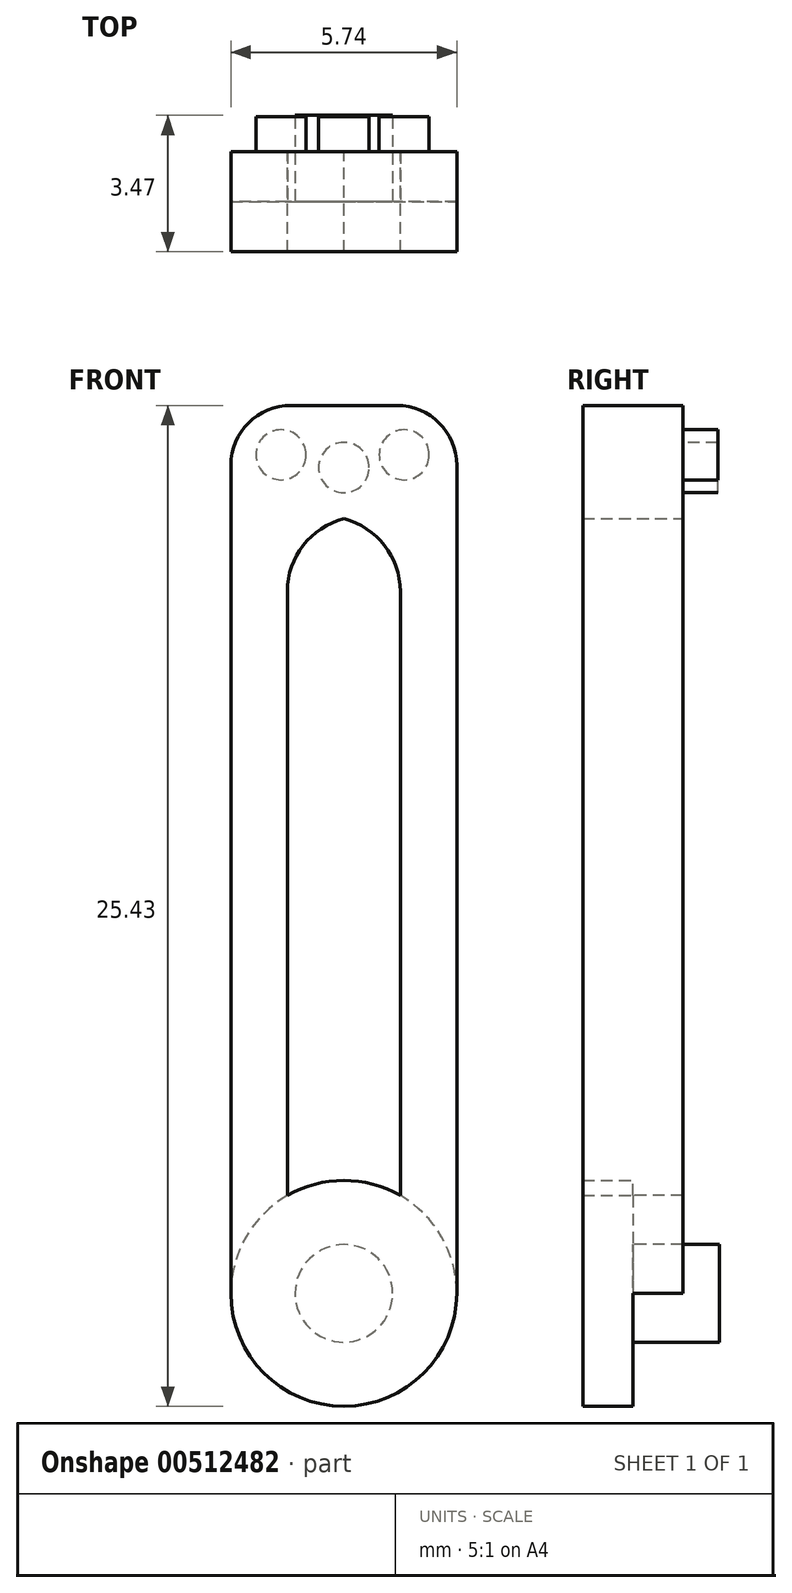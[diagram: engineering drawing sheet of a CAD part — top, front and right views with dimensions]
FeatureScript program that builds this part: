
annotation { "Feature Type Name" : "Feature", "Feature Type Description" : "" }
export const myFeature = defineFeature(function(context is Context, id is Id, definition is map)
    precondition{}
    {
        {
            var Q0;
            Q0=qCreatedBy(makeId("Front.planeOp"),FACE);
            var sketch = newSketch(context, id + "F0", { "sketchPlane" : qUnion([Q0])});
            skCircle(sketch, "E0", {"center": v(0, 2.87) * mm, "radius": 2.87 * mm});
            skLineSegment(sketch, "E1", {"start": v(0, 25.43) * mm, "end": v(2.87, 25.43) * mm});
            skLineSegment(sketch, "E2", {"start": v(2.87, 25.43) * mm, "end": v(2.87, 2.87) * mm});
            skLineSegment(sketch, "E3", {"start": v(-2.87, 2.87) * mm, "end": v(-2.87, 25.43) * mm});
            skLineSegment(sketch, "E4", {"start": v(-2.87, 25.43) * mm, "end": v(2.87, 25.43) * mm});
            skLineSegment(sketch, "E5", {"start": v(-2.87, 25.43) * mm, "end": v(0, 25.43) * mm});
            skLineSegment(sketch, "E6", {"start": v(-2.87, 25.43) * mm, "end": v(-1.43, 25.43) * mm});
            skLineSegment(sketch, "E7", {"start": v(1.43, 5.35) * mm, "end": v(1.43, 22.6) * mm});
            skLineSegment(sketch, "E8", {"start": v(-1.43, 5.35) * mm, "end": v(-1.43, 22.6) * mm});
            skLineSegment(sketch, "E9", {"start": v(-1.43, 22.6) * mm, "end": v(1.43, 22.6) * mm});
            skSolve(sketch);
        }
        {
            var Q0;
            {var subQ0=sQuery(id+"F0.wireOp",EDGE,"E2");Q0=makeQuery(id+"F0.imprint","IMPRINT",FACE,{"disambiguationData":[TD([[makeQuery(id+"F0.imprint","IMPRINT",EDGE,{"derivedFrom":subQ0}),-1.0]])]});}
            var Q1;
            {var subQ0=sQuery(id+"F0.wireOp",EDGE,"E0");var subQ1=makeQuery(id+"F0.imprint","INTERSECT",VERTEX,{"derivedFrom":[subQ0,sQuery(id+"F0.wireOp",EDGE,"E2")]});Q1=makeQuery(id+"F0.imprint","IMPRINT",FACE,{"disambiguationData":[TD([[makeQuery(id+"F0.imprint","IMPRINT",EDGE,{"disambiguationData":[TD([[subQ1,-1.0]])],"derivedFrom":subQ0}),1.0]])]});}
            extrude(context, id + "F1", {"entities" : qUnion([Q0, Q1]), "depth" : 1.27 * mm});
        }
        {
            var Q0;
            Q0=makeQuery(id+"F1.opExtrude","CAP_FACE",FACE,{"disambiguationData":[OSD([sQuery(id+"F0.wireOp",EDGE,"E0"),sQuery(id+"F0.wireOp",EDGE,"E2"),sQuery(id+"F0.wireOp",EDGE,"E3"),sQuery(id+"F0.wireOp",EDGE,"E4"),sQuery(id+"F0.wireOp",EDGE,"E5"),sQuery(id+"F0.wireOp",EDGE,"E6"),sQuery(id+"F0.wireOp",EDGE,"E7"),sQuery(id+"F0.wireOp",EDGE,"E8"),sQuery(id+"F0.wireOp",EDGE,"E9")])],"isStart":true});
            var sketch = newSketch(context, id + "F2", { "sketchPlane" : qUnion([Q0])});
            skCircle(sketch, "E10", {"center": v(0, 2.87) * mm, "radius": 1.24 * mm});
            skSolve(sketch);
        }
        {
            var Q0;
            Q0=makeQuery(id+"F1.opExtrude","SWEPT_EDGE",EDGE,{"disambiguationData":[OSD([sQuery(id+"F0.wireOp",EDGE,"E2"),sQuery(id+"F0.wireOp",EDGE,"E4")])]});
            var Q1;
            Q1=makeQuery(id+"F1.opExtrude","SWEPT_EDGE",EDGE,{"disambiguationData":[OSD([sQuery(id+"F0.wireOp",EDGE,"E3"),sQuery(id+"F0.wireOp",EDGE,"E6")])]});
            fillet(context, id + "F3", {"entities" : qUnion([Q0, Q1]), "radius" : 1.52 * mm, "tangentPropagation" : true, "allowEdgeOverflow" : false});
        }
        {
            var Q0;
            Q0=makeQuery(id+"F1.opExtrude","CAP_FACE",FACE,{"disambiguationData":[OSD([sQuery(id+"F0.wireOp",EDGE,"E0"),sQuery(id+"F0.wireOp",EDGE,"E2"),sQuery(id+"F0.wireOp",EDGE,"E3"),sQuery(id+"F0.wireOp",EDGE,"E4"),sQuery(id+"F0.wireOp",EDGE,"E5"),sQuery(id+"F0.wireOp",EDGE,"E6"),sQuery(id+"F0.wireOp",EDGE,"E7"),sQuery(id+"F0.wireOp",EDGE,"E8"),sQuery(id+"F0.wireOp",EDGE,"E9")])],"isStart":false});
            var sketch = newSketch(context, id + "F4", { "sketchPlane" : qUnion([Q0])});
            skPoint(sketch, "E11.startSnap0", {"position": v(-1.21, 23.8) * mm});
            skCircle(sketch, "E12", {"center": v(-1.6, 24.17) * mm, "radius": 0.64 * mm});
            skCircle(sketch, "E13", {"center": v(1.53, 24.17) * mm, "radius": 0.64 * mm});
            skCircle(sketch, "E14", {"center": v(0, 23.85) * mm, "radius": 0.64 * mm});
            skSolve(sketch);
        }
        {
            var Q0;
            Q0=makeQuery(id+"F1.opExtrude","SWEPT_EDGE",EDGE,{"disambiguationData":[OSD([sQuery(id+"F0.wireOp",EDGE,"E7"),sQuery(id+"F0.wireOp",EDGE,"E9")])]});
            var Q1;
            Q1=makeQuery(id+"F1.opExtrude","SWEPT_EDGE",EDGE,{"disambiguationData":[OSD([sQuery(id+"F0.wireOp",EDGE,"E8"),sQuery(id+"F0.wireOp",EDGE,"E9")])]});
            fillet(context, id + "F5", {"entities" : qUnion([Q0, Q1]), "radius" : 1.9 * mm, "tangentPropagation" : true, "allowEdgeOverflow" : false});
        }
        {
            var Q0;
            Q0 = qSketchRegion(id + "F2", true);
            extrude(context, id + "F6", {"entities" : qUnion([Q0]), "operationType" : NewBodyOperationType.ADD, "depth" : 2.2 * mm});
        }
        {
            var Q0;
            Q0 = qSketchRegion(id + "F4", true);
            extrude(context, id + "F7", {"entities" : qUnion([Q0]), "operationType" : NewBodyOperationType.ADD, "depth" : -3.43 * mm});
        }
        {
            var Q0;
            Q0=makeQuery(id+"F1.opExtrude","CAP_FACE",FACE,{"disambiguationData":[OSD([sQuery(id+"F0.wireOp",EDGE,"E0"),sQuery(id+"F0.wireOp",EDGE,"E2"),sQuery(id+"F0.wireOp",EDGE,"E3"),sQuery(id+"F0.wireOp",EDGE,"E4"),sQuery(id+"F0.wireOp",EDGE,"E5"),sQuery(id+"F0.wireOp",EDGE,"E6"),sQuery(id+"F0.wireOp",EDGE,"E7"),sQuery(id+"F0.wireOp",EDGE,"E8"),sQuery(id+"F0.wireOp",EDGE,"E9")])],"isStart":false});
            var sketch = newSketch(context, id + "F8", { "sketchPlane" : qUnion([Q0])});
            skCircle(sketch, "E15", {"center": v(0, 2.87) * mm, "radius": 2.87 * mm});
            skCircle(sketch, "E16", {"center": v(-1.34, 23.9) * mm, "radius": 1.52 * mm});
            skCircle(sketch, "E17", {"center": v(1.34, 23.9) * mm, "radius": 1.52 * mm});
            skLineSegment(sketch, "E18", {"start": v(-1.34, 25.43) * mm, "end": v(1.34, 25.43) * mm});
            skLineSegment(sketch, "E19", {"start": v(-2.87, 22.55) * mm, "end": v(-2.87, 2.87) * mm});
            skLineSegment(sketch, "E20", {"start": v(2.87, 2.87) * mm, "end": v(2.87, 23.9) * mm});
            skLineSegment(sketch, "E21", {"start": v(-1.43, 5.35) * mm, "end": v(-1.43, 20.7) * mm});
            skLineSegment(sketch, "E22", {"start": v(1.43, 5.35) * mm, "end": v(1.43, 20.7) * mm});
            skSolve(sketch);
        }
        {
            var Q0;
            {var subQ8=sQuery(id+"F8.wireOp",EDGE,"E19");Q0=makeQuery(id+"F8.imprint","IMPRINT",FACE,{"disambiguationData":[TD([[makeQuery(id+"F8.imprint","IMPRINT",EDGE,{"derivedFrom":subQ8}),-1.0]])]});}
            var Q1;
            {var subQ0=sQuery(id+"F8.wireOp",EDGE,"E16");var subQ1=makeQuery(id+"F8.imprint","INTERSECT",VERTEX,{"derivedFrom":[subQ0,sQuery(id+"F8.wireOp",EDGE,"E18")]});Q1=makeQuery(id+"F8.imprint","IMPRINT",FACE,{"disambiguationData":[TD([[makeQuery(id+"F8.imprint","IMPRINT",EDGE,{"disambiguationData":[TD([[subQ1,1.0]])],"derivedFrom":subQ0}),1.0]])]});}
            var Q2;
            {var subQ0=sQuery(id+"F8.wireOp",EDGE,"E17");var subQ1=sQuery(id+"F8.wireOp",EDGE,"E16");var subQ2=makeQuery(id+"F8.imprint","INTERSECT",VERTEX,{"disambiguationData":[OD(0.0)],"derivedFrom":[subQ1,subQ0]});Q2=makeQuery(id+"F8.imprint","IMPRINT",FACE,{"disambiguationData":[TD([[makeQuery(id+"F8.imprint","IMPRINT",EDGE,{"disambiguationData":[TD([[subQ2,1.0]])],"derivedFrom":subQ1}),-1.0]])]});}
            var Q3;
            {var subQ0=sQuery(id+"F8.wireOp",EDGE,"E17");var subQ1=sQuery(id+"F8.wireOp",EDGE,"E16");var subQ2=makeQuery(id+"F8.imprint","INTERSECT",VERTEX,{"disambiguationData":[OD(0.0)],"derivedFrom":[subQ1,subQ0]});Q3=makeQuery(id+"F8.imprint","IMPRINT",FACE,{"disambiguationData":[TD([[makeQuery(id+"F8.imprint","IMPRINT",EDGE,{"disambiguationData":[TD([[subQ2,1.0]])],"derivedFrom":subQ1}),1.0]])]});}
            var Q4;
            {var subQ0=sQuery(id+"F8.wireOp",EDGE,"E18");Q4=makeQuery(id+"F8.imprint","IMPRINT",FACE,{"disambiguationData":[TD([[makeQuery(id+"F8.imprint","IMPRINT",EDGE,{"derivedFrom":subQ0}),-1.0]])]});}
            extrude(context, id + "F9", {"entities" : qUnion([Q0, Q1, Q2, Q3, Q4]), "operationType" : NewBodyOperationType.ADD, "depth" : -2.54 * mm});
        }
    });
